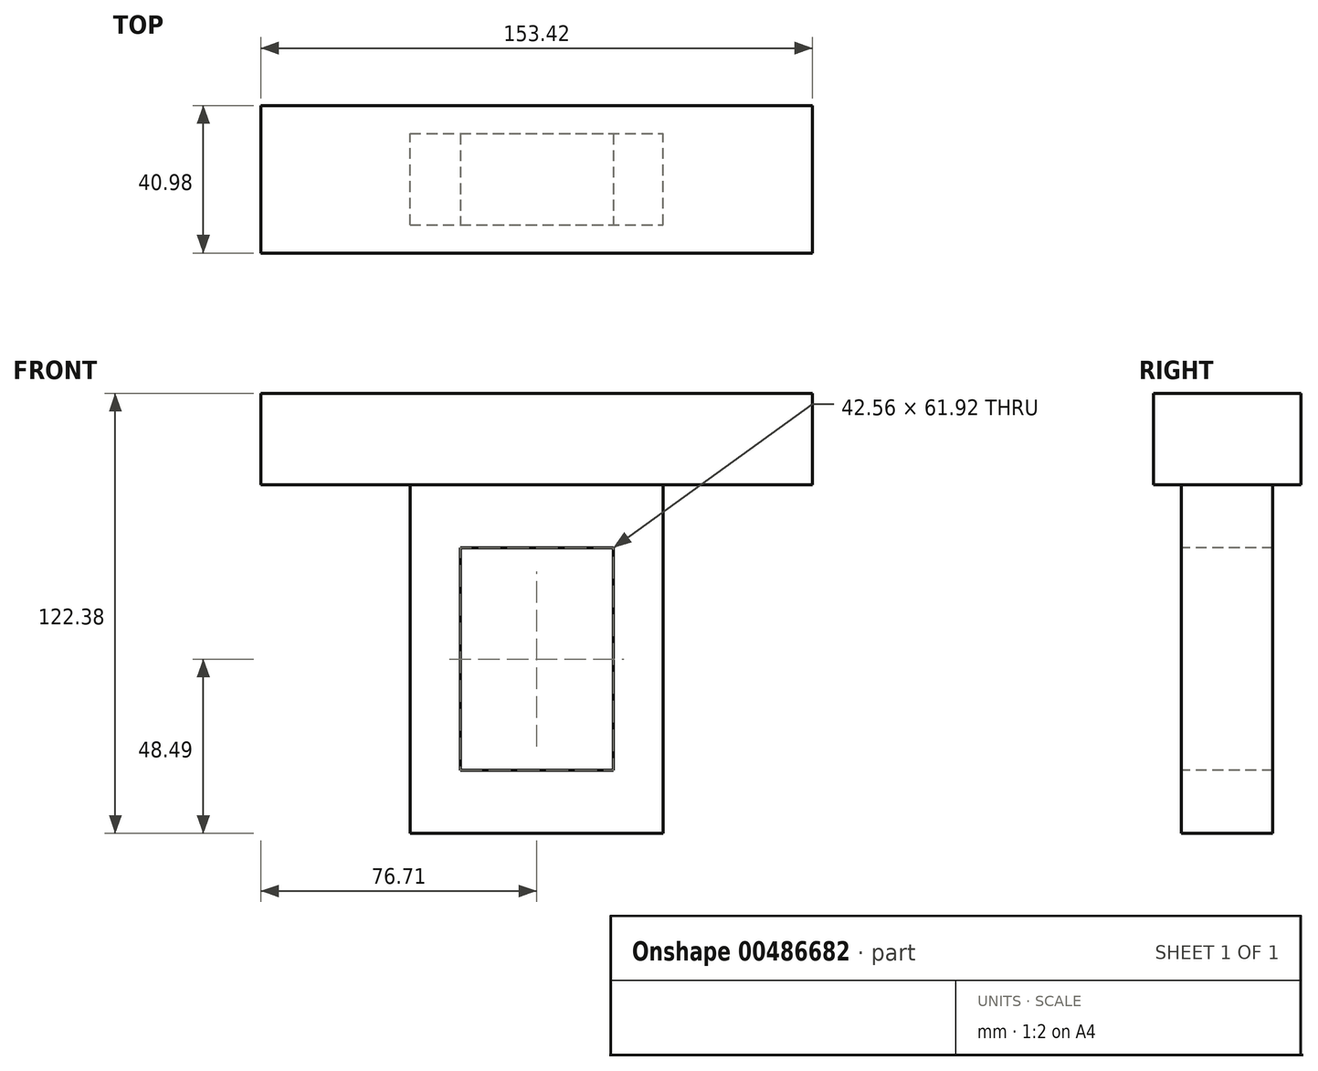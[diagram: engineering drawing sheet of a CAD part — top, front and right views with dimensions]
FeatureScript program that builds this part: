
annotation { "Feature Type Name" : "Feature", "Feature Type Description" : "" }
export const myFeature = defineFeature(function(context is Context, id is Id, definition is map)
    precondition{}
    {
        {
            var Q0;
            Q0=qCreatedBy(makeId("Front.planeOp"),FACE);
            var sketch = newSketch(context, id + "F0", { "sketchPlane" : qUnion([Q0])});
            skLineSegment(sketch, "E0.bottom", {"start": v(-35.21, 48.49) * mm, "end": v(35.21, 48.49) * mm});
            skLineSegment(sketch, "E0.top", {"start": v(-35.21, -48.49) * mm, "end": v(35.21, -48.49) * mm});
            skLineSegment(sketch, "E0.left", {"start": v(-35.21, 48.49) * mm, "end": v(-35.21, -48.49) * mm});
            skLineSegment(sketch, "E0.right", {"start": v(35.21, 48.49) * mm, "end": v(35.21, -48.49) * mm});
            skPoint(sketch, "E0.middle", {"position": v(0, 0) * mm});
            skSolve(sketch);
        }
        {
            var Q0;
            Q0=makeQuery(id+"F0.imprint","IMPRINT",FACE,{"disambiguationData":[TD([[makeQuery(id+"F0.imprint","IMPRINT",EDGE,{"derivedFrom":sQuery(id+"F0.wireOp",EDGE,"E0.bottom")}),-1.0]])]});
            extrude(context, id + "F1", {"entities" : qUnion([Q0]), "depth" : 25.4 * mm});
        }
        {
            var Q0;
            Q0=makeQuery(id+"F1.opExtrude","SWEPT_FACE",FACE,{"disambiguationData":[OSD([sQuery(id+"F0.wireOp",EDGE,"E0.bottom")])]});
            var sketch = newSketch(context, id + "F2", { "sketchPlane" : qUnion([Q0])});
            skLineSegment(sketch, "E1.bottom", {"start": v(-76.71, 7.79) * mm, "end": v(76.71, 7.79) * mm});
            skLineSegment(sketch, "E1.top", {"start": v(-76.71, -33.19) * mm, "end": v(76.71, -33.19) * mm});
            skLineSegment(sketch, "E1.left", {"start": v(-76.71, 7.79) * mm, "end": v(-76.71, -33.19) * mm});
            skLineSegment(sketch, "E1.right", {"start": v(76.71, 7.79) * mm, "end": v(76.71, -33.19) * mm});
            skPoint(sketch, "E1.middle", {"position": v(0, -12.7) * mm});
            skPoint(sketch, "E1.middle.positionSnap0", {"position": v(-35.21, -12.7) * mm});
            skPoint(sketch, "E1.centerSnap0", {"position": v(-35.21, -12.7) * mm});
            skSolve(sketch);
        }
        {
            var Q0;
            Q0=makeQuery(id+"F2.imprint","IMPRINT",FACE,{"disambiguationData":[TD([[makeQuery(id+"F2.imprint","IMPRINT",EDGE,{"derivedFrom":sQuery(id+"F2.wireOp",EDGE,"E1.bottom")}),-1.0]])]});
            var Q1;
            {var subQ0=sQuery(id+"F0.wireOp",EDGE,"E0.bottom");Q1=makeQuery(id+"F2.imprint","IMPRINT",FACE,{"disambiguationData":[TD([[makeQuery(id+"F2.imprint","IMPRINT",EDGE,{"derivedFrom":makeQuery(id+"F1.opExtrude","CAP_EDGE",EDGE,{"disambiguationData":[OSD([subQ0])],"isStart":true})}),-1.0]])]});}
            extrude(context, id + "F3", {"entities" : qUnion([Q0, Q1]), "operationType" : NewBodyOperationType.ADD, "depth" : 25.4 * mm});
        }
        {
            var Q0;
            Q0=makeQuery(id+"F1.opExtrude","CAP_FACE",FACE,{"disambiguationData":[OSD([sQuery(id+"F0.wireOp",EDGE,"E0.bottom"),sQuery(id+"F0.wireOp",EDGE,"E0.top"),sQuery(id+"F0.wireOp",EDGE,"E0.left"),sQuery(id+"F0.wireOp",EDGE,"E0.right")])],"isStart":false});
            var sketch = newSketch(context, id + "F4", { "sketchPlane" : qUnion([Q0])});
            skLineSegment(sketch, "E2.bottom", {"start": v(-21.28, 30.96) * mm, "end": v(21.28, 30.96) * mm});
            skLineSegment(sketch, "E2.top", {"start": v(-21.28, -30.96) * mm, "end": v(21.28, -30.96) * mm});
            skLineSegment(sketch, "E2.left", {"start": v(-21.28, 30.96) * mm, "end": v(-21.28, -30.96) * mm});
            skLineSegment(sketch, "E2.right", {"start": v(21.28, 30.96) * mm, "end": v(21.28, -30.96) * mm});
            skPoint(sketch, "E2.middle", {"position": v(0, 0) * mm});
            skSolve(sketch);
        }
        {
            var Q0;
            Q0=makeQuery(id+"F4.imprint","IMPRINT",FACE,{"disambiguationData":[TD([[makeQuery(id+"F4.imprint","IMPRINT",EDGE,{"derivedFrom":sQuery(id+"F4.wireOp",EDGE,"E2.bottom")}),-1.0]])]});
            extrude(context, id + "F5", {"entities" : qUnion([Q0]), "operationType" : NewBodyOperationType.REMOVE, "oppositeDirection" : true, "depth" : 25.4 * mm});
        }
    });
